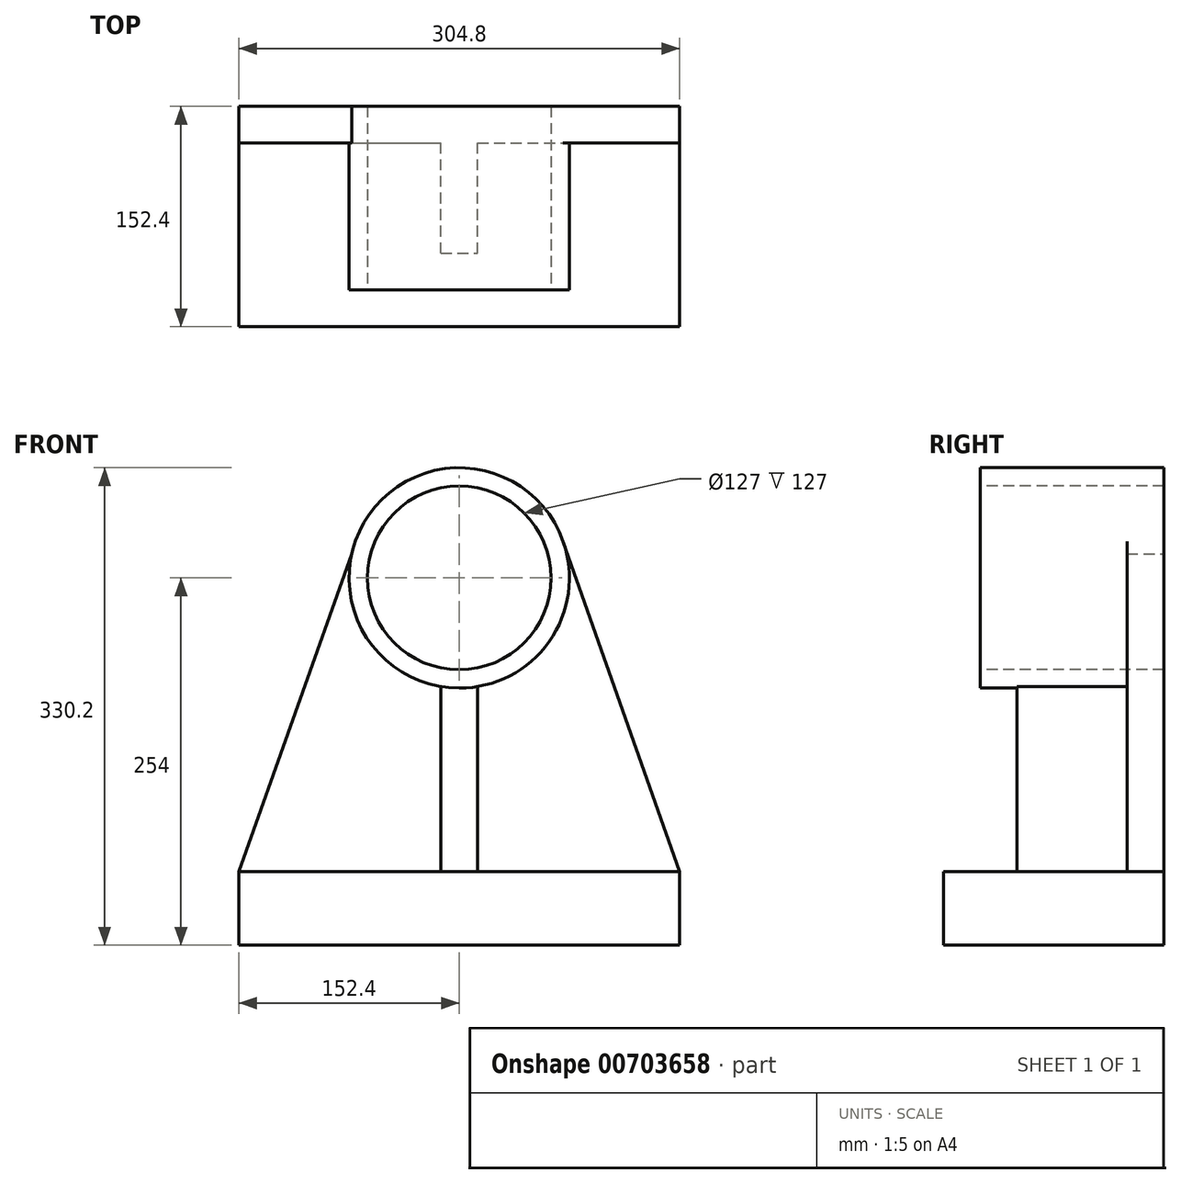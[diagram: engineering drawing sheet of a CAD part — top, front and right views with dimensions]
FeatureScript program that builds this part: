
annotation { "Feature Type Name" : "Feature", "Feature Type Description" : "" }
export const myFeature = defineFeature(function(context is Context, id is Id, definition is map)
    precondition{}
    {
        {
            var Q0;
            Q0=qCreatedBy(makeId("Front.planeOp"),FACE);
            var sketch = newSketch(context, id + "F0", { "sketchPlane" : qUnion([Q0])});
            skLineSegment(sketch, "E0.bottom", {"start": v(-152.4, -50.8) * mm, "end": v(152.4, -50.8) * mm});
            skLineSegment(sketch, "E0.top", {"start": v(-152.4, 0) * mm, "end": v(152.4, 0) * mm});
            skLineSegment(sketch, "E0.left", {"start": v(-152.4, -50.8) * mm, "end": v(-152.4, 0) * mm});
            skLineSegment(sketch, "E0.right", {"start": v(152.4, -50.8) * mm, "end": v(152.4, 0) * mm});
            skCircle(sketch, "E1", {"center": v(0, 203.2) * mm, "radius": 76.2 * mm});
            skLineSegment(sketch, "E2", {"start": v(152.4, 0) * mm, "end": v(68.57, 237.9) * mm});
            skLineSegment(sketch, "E3", {"start": v(-152.4, 0) * mm, "end": v(-68.24, 237.1) * mm});
            skLineSegment(sketch, "E4", {"start": v(12.7, 0) * mm, "end": v(12.7, 128.07) * mm});
            skLineSegment(sketch, "E5", {"start": v(-12.7, 0) * mm, "end": v(-12.7, 128.07) * mm});
            skSolve(sketch);
        }
        {
            var Q0;
            Q0=makeQuery(id+"F0.imprint","IMPRINT",FACE,{"disambiguationData":[TD([[makeQuery(id+"F0.imprint","IMPRINT",EDGE,{"derivedFrom":sQuery(id+"F0.wireOp",EDGE,"E0.bottom")}),1.0]])]});
            extrude(context, id + "F1", {"entities" : qUnion([Q0]), "depth" : 152.4 * mm, "offsetDistance" : 25.4 * mm});
        }
        {
            var Q0;
            Q0 = qSketchRegion(id + "F0", true);
            extrude(context, id + "F2", {"entities" : qUnion([Q0]), "operationType" : NewBodyOperationType.ADD, "depth" : 25.4 * mm, "offsetDistance" : 25.4 * mm});
        }
        {
            var Q0;
            Q0=makeQuery(id+"F2.opExtrude","CAP_FACE",FACE,{"disambiguationData":[OSD([sQuery(id+"F0.wireOp",EDGE,"E0.bottom"),sQuery(id+"F0.wireOp",EDGE,"E0.top"),sQuery(id+"F0.wireOp",EDGE,"E0.left"),sQuery(id+"F0.wireOp",EDGE,"E0.right"),sQuery(id+"F0.wireOp",EDGE,"E1"),sQuery(id+"F0.wireOp",EDGE,"E2"),sQuery(id+"F0.wireOp",EDGE,"E3"),sQuery(id+"F0.wireOp",EDGE,"E4"),sQuery(id+"F0.wireOp",EDGE,"E5")])],"isStart":false});
            var sketch = newSketch(context, id + "F3", { "sketchPlane" : qUnion([Q0])});
            skCircle(sketch, "E6", {"center": v(0, 203.2) * mm, "radius": 76.2 * mm});
            skSolve(sketch);
        }
        {
            var Q0;
            {var subQ0=sQuery(id+"F3.wireOp",EDGE,"E6");var subQ1=makeQuery(id+"F3.imprint","INTERSECT",VERTEX,{"derivedFrom":[makeQuery(id+"F2.opExtrude","CAP_EDGE",EDGE,{"disambiguationData":[OSD([sQuery(id+"F0.wireOp",EDGE,"E2")])],"isStart":false}),subQ0]});Q0=makeQuery(id+"F3.imprint","IMPRINT",FACE,{"disambiguationData":[TD([[makeQuery(id+"F3.imprint","IMPRINT",EDGE,{"disambiguationData":[TD([[subQ1,-1.0]])],"derivedFrom":subQ0}),1.0]])]});}
            extrude(context, id + "F4", {"entities" : qUnion([Q0]), "operationType" : NewBodyOperationType.ADD, "depth" : 101.6 * mm, "offsetDistance" : 25.4 * mm});
        }
        {
            var Q0;
            Q0=qCreatedBy(makeId("Front.planeOp"),FACE);
            var sketch = newSketch(context, id + "F5", { "sketchPlane" : qUnion([Q0])});
            skLineSegment(sketch, "E7.bottom", {"start": v(-12.7, 0) * mm, "end": v(12.7, 0) * mm});
            skLineSegment(sketch, "E7.top", {"start": v(-12.7, 129.54) * mm, "end": v(12.7, 129.54) * mm});
            skLineSegment(sketch, "E7.left", {"start": v(-12.7, 0) * mm, "end": v(-12.7, 129.54) * mm});
            skLineSegment(sketch, "E7.right", {"start": v(12.7, 0) * mm, "end": v(12.7, 129.54) * mm});
            skSolve(sketch);
        }
        {
            var Q0;
            Q0 = qSketchRegion(id + "F5", true);
            extrude(context, id + "F6", {"entities" : qUnion([Q0]), "operationType" : NewBodyOperationType.ADD, "depth" : 101.6 * mm, "offsetDistance" : 25.4 * mm});
        }
        {
            var Q0;
            Q0=makeQuery(id+"F4.opExtrude","CAP_FACE",FACE,{"disambiguationData":[OSD([sQuery(id+"F3.wireOp",EDGE,"E6")])],"isStart":false});
            var sketch = newSketch(context, id + "F7", { "sketchPlane" : qUnion([Q0])});
            skCircle(sketch, "E8", {"center": v(0, 203.2) * mm, "radius": 63.5 * mm});
            skSolve(sketch);
        }
        {
            var Q0;
            Q0=makeQuery(id+"F7.imprint","IMPRINT",FACE,{"disambiguationData":[TD([[makeQuery(id+"F7.imprint","IMPRINT",EDGE,{"derivedFrom":sQuery(id+"F7.wireOp",EDGE,"E8")}),1.0]])]});
            extrude(context, id + "F8", {"entities" : qUnion([Q0]), "operationType" : NewBodyOperationType.REMOVE, "endBound" : BoundingType.THROUGH_ALL, "oppositeDirection" : true, "depth" : 25.4 * mm, "offsetDistance" : 25.4 * mm});
        }
    });
